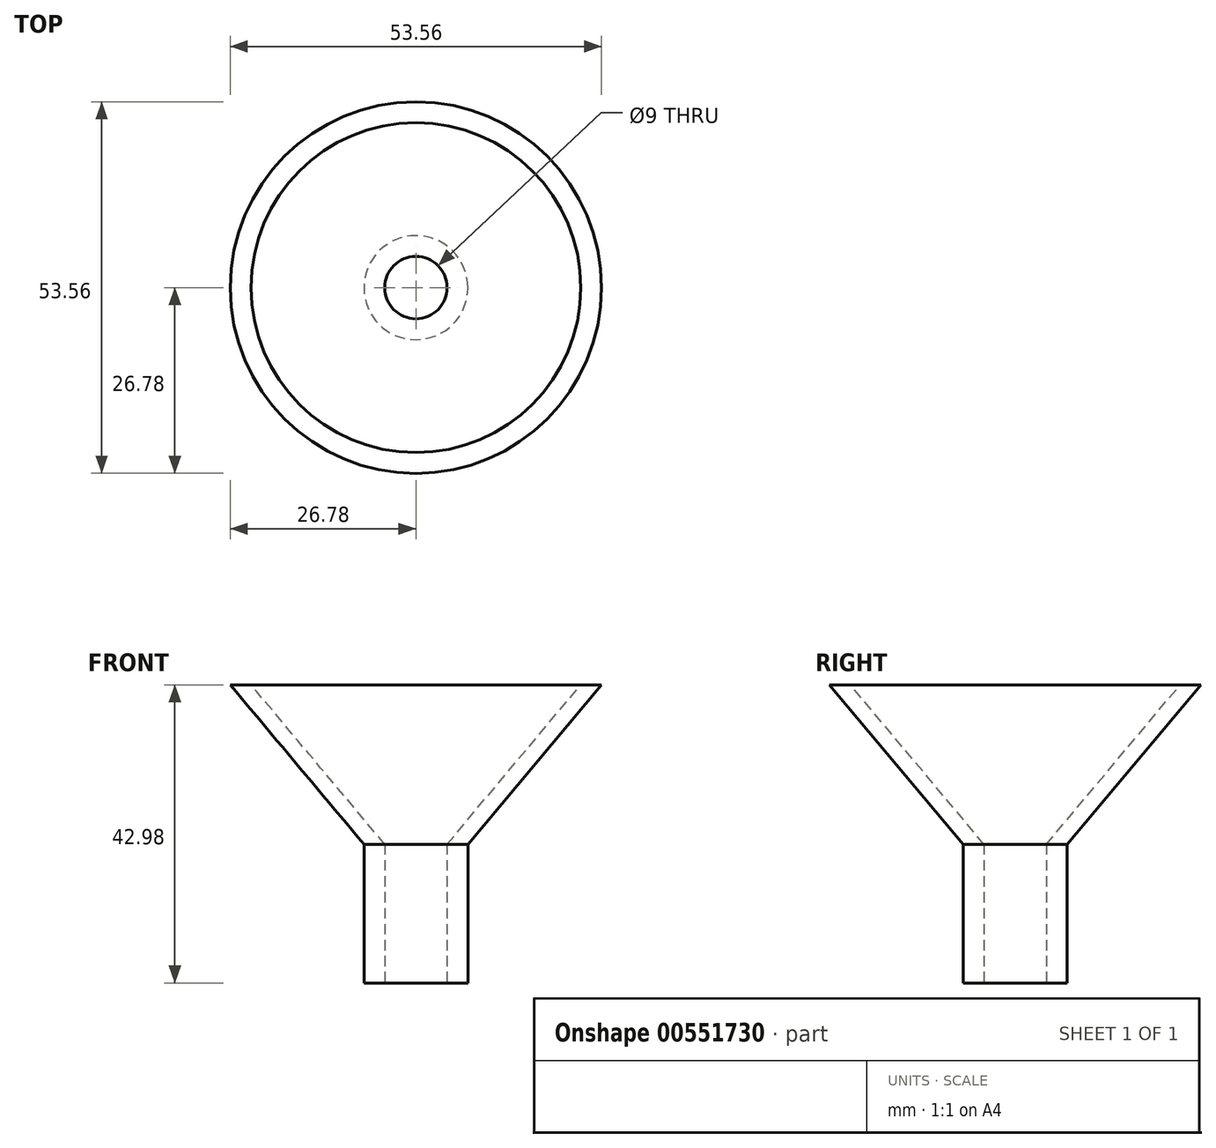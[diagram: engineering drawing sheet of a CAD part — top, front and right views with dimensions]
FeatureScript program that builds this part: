
annotation { "Feature Type Name" : "Feature", "Feature Type Description" : "" }
export const myFeature = defineFeature(function(context is Context, id is Id, definition is map)
    precondition{}
    {
        {
            var Q0;
            Q0=qCreatedBy(makeId("Front.planeOp"),FACE);
            var sketch = newSketch(context, id + "F0", { "sketchPlane" : qUnion([Q0])});
            skLineSegment(sketch, "E0", {"start": v(0, 0) * mm, "end": v(-3, 0) * mm});
            skLineSegment(sketch, "E1", {"start": v(-3, 0) * mm, "end": v(-3, 20) * mm});
            skLineSegment(sketch, "E2", {"start": v(-3, 20) * mm, "end": v(-22.28, 42.98) * mm});
            skLineSegment(sketch, "E3", {"start": v(-22.28, 42.98) * mm, "end": v(-19.28, 42.98) * mm});
            skLineSegment(sketch, "E4", {"start": v(-19.28, 42.98) * mm, "end": v(0, 20) * mm});
            skLineSegment(sketch, "E5", {"start": v(0, 20) * mm, "end": v(0, 0) * mm});
            skLineSegment(sketch, "E6", {"start": v(0, 0) * mm, "end": v(4.5, 0) * mm, "construction": true});
            skLineSegment(sketch, "E7", {"start": v(4.5, 0) * mm, "end": v(4.5, 9.66) * mm, "construction": true});
            skSolve(sketch);
        }
        {
            var Q0;
            Q0=makeQuery(id+"F0.imprint","IMPRINT",FACE,{"disambiguationData":[TD([[makeQuery(id+"F0.imprint","IMPRINT",EDGE,{"derivedFrom":sQuery(id+"F0.wireOp",EDGE,"E0")}),-1.0]])]});
            var Q1;
            Q1=sQuery(id+"F0.wireOp",EDGE,"E7");
            revolve(context, id + "F1", {"entities" : qUnion([Q0]), "axis" : qUnion([Q1]), "revolveType" : RevolveType.FULL});
        }
    });
